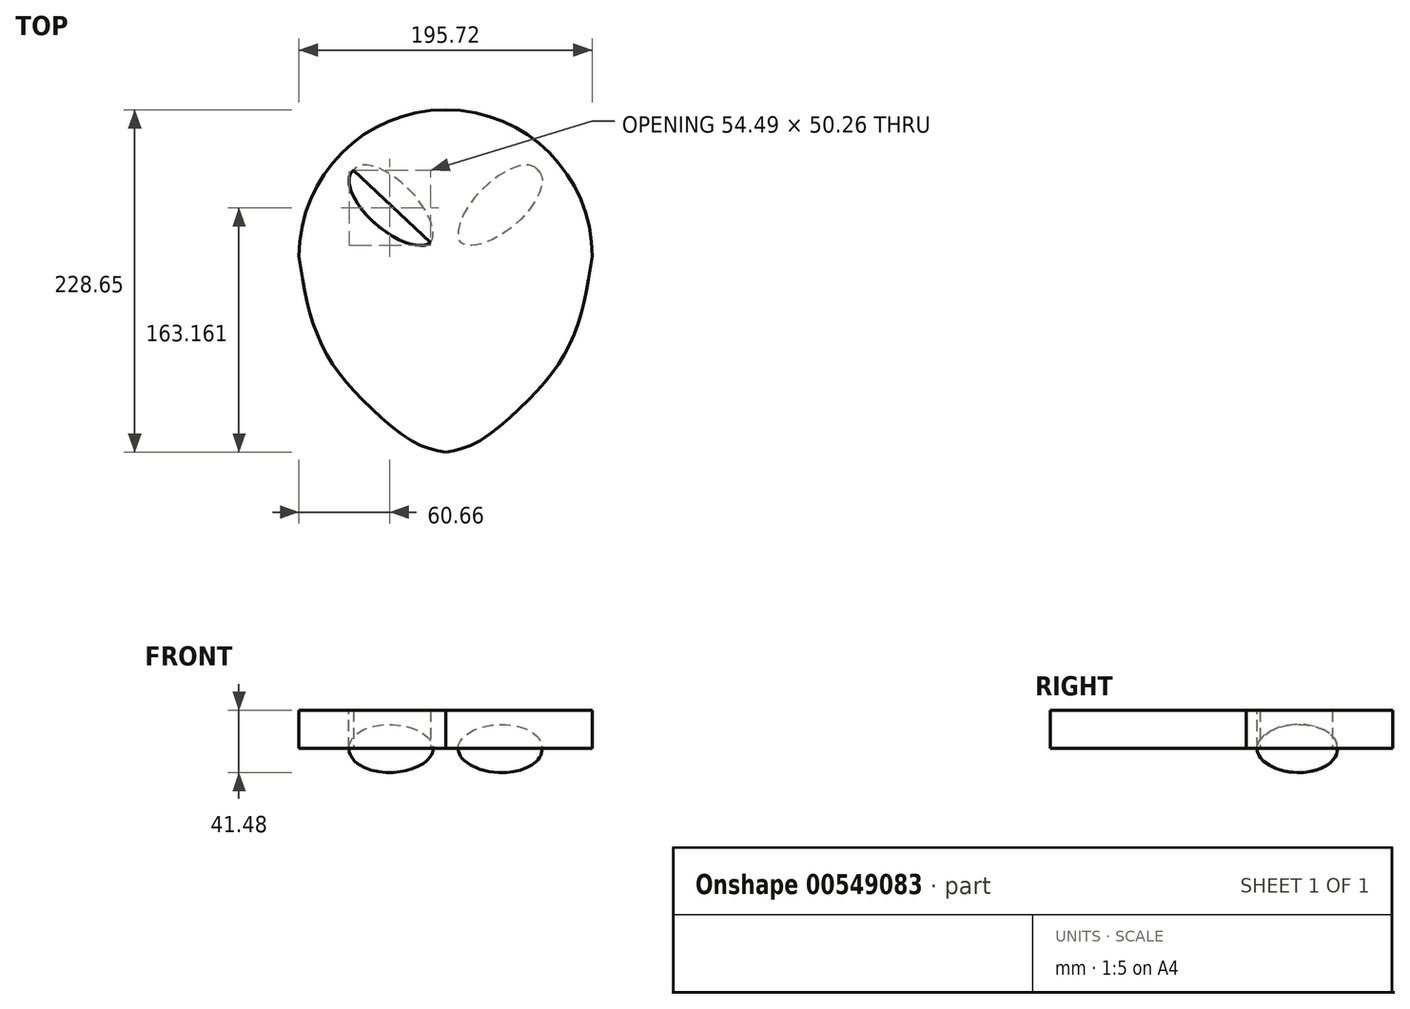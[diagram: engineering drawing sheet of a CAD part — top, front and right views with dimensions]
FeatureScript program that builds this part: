
annotation { "Feature Type Name" : "Feature", "Feature Type Description" : "" }
export const myFeature = defineFeature(function(context is Context, id is Id, definition is map)
    precondition{}
    {
        {
            var Q0;
            Q0=qCreatedBy(makeId("Top.planeOp"),FACE);
            var sketch = newSketch(context, id + "F0", { "sketchPlane" : qUnion([Q0])});
            skArc(sketch, "E0", {"start": v(0, 97.86) * mm, "mid": v(-69.2, 69.2) * mm, "end": v(-97.86, 0) * mm});
            skLineSegment(sketch, "E1", {"start": v(0, 0) * mm, "end": v(0, 109.73) * mm});
            skLineSegment(sketch, "E2", {"start": v(0, 109.73) * mm, "end": v(0, -174.91) * mm});
            skLineSegment(sketch, "E3", {"start": v(0, 0) * mm, "end": v(-144.15, 0) * mm});
            skFitSpline(sketch, "E4", {"points": [v(-97.86, 0) * mm, v(-91.17, -35.57) * mm, v(-77.77, -68.42) * mm, v(-54.28, -96.83) * mm, v(-20.67, -124.27) * mm, v(0, -130.79) * mm], "startDerivative": vector(26.77, -174.19) * mm, "endDerivative": vector(124.04, -23.27) * mm});
            skLineSegment(sketch, "E5", {"start": v(0, 0) * mm, "end": v(-71.52, 66.8) * mm});
            skEllipticalArc(sketch, "E6", {});
            skArc(sketch, "E7.MirrorCS", {"start": v(0, 97.86) * mm, "mid": v(69.2, 69.2) * mm, "end": v(97.86, 0) * mm});
            skFitSpline(sketch, "E8.MirrorCS", {"points": [v(97.86, 0) * mm, v(91.17, -35.57) * mm, v(77.77, -68.42) * mm, v(54.28, -96.83) * mm, v(20.67, -124.27) * mm, v(0, -130.79) * mm], "startDerivative": vector(-26.77, -174.19) * mm, "endDerivative": vector(-124.04, -23.27) * mm});
            const initialGuessF0  = {"E6": [-0.03575795501772881, 0.03339906463104727, -0.7558408878657595, 0.6547553376875216, 0.03540696900584423, 0.016033265241295534, 6.200646879437301, 3.059054225847506]};
            skSetInitialGuess(sketch, initialGuessF0);
            skSolve(sketch);
        }
        {
            var Q0;
            {var subQ0=sQuery(id+"F0.wireOp",EDGE,"E6");Q0=makeQuery(id+"F0.imprint","IMPRINT",FACE,{"disambiguationData":[TD([[makeQuery(id+"F0.imprint","IMPRINT",EDGE,{"derivedFrom":subQ0}),1.0]])]});}
            var Q1;
            Q1=sQuery(id+"F0.wireOp",EDGE,"E5");
            revolve(context, id + "F1", {"entities" : qUnion([Q0]), "axis" : qUnion([Q1]), "revolveType" : RevolveType.FULL});
        }
        {
            var Q0;
            Q0=makeQuery(id+"F1.opRevolve","SWEPT_BODY",BODY,{"disambiguationData":[OSD([sQuery(id+"F0.wireOp",EDGE,"E5"),sQuery(id+"F0.wireOp",EDGE,"E6")])]});
            var Q1;
            Q1=qCreatedBy(makeId("Right.planeOp"),FACE);
            mirror(context, id + "F2", {"entities" : qUnion([Q0]), "mirrorPlane" : qUnion([Q1])});
        }
        {
            var Q0;
            Q0 = qSketchRegion(id + "F0", true);
            extrude(context, id + "F3", {"entities" : qUnion([Q0]), "depth" : 25.4 * mm, "offsetDistance" : 25.4 * mm});
        }
    });
